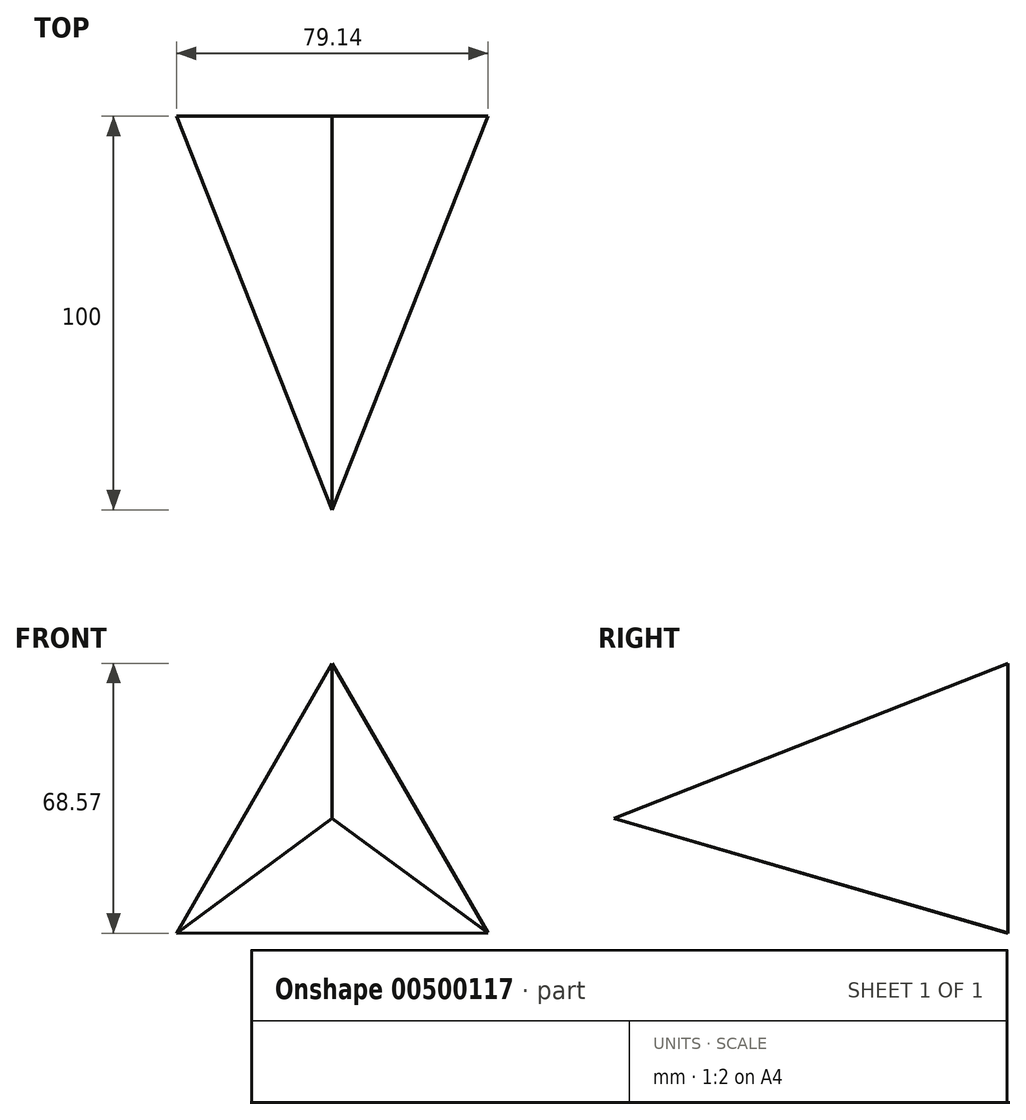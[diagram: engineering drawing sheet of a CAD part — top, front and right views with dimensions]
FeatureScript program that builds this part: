
annotation { "Feature Type Name" : "Feature", "Feature Type Description" : "" }
export const myFeature = defineFeature(function(context is Context, id is Id, definition is map)
    precondition{}
    {
        {
            var Q0;
            Q0=qCreatedBy(makeId("Front.planeOp"),FACE);
            var sketch = newSketch(context, id + "F0", { "sketchPlane" : qUnion([Q0])});
            skCircle(sketch, "E0.cCircle", {"center": v(0, 0) * mm, "radius": 45.69 * mm, "construction": true});
            skLineSegment(sketch, "E0.0", {"start": v(-0.04, 45.69) * mm, "end": v(39.6, -22.8) * mm});
            skLineSegment(sketch, "E0.1", {"start": v(39.6, -22.8) * mm, "end": v(-39.55, -22.88) * mm});
            skLineSegment(sketch, "E0.2", {"start": v(-39.55, -22.88) * mm, "end": v(-0.04, 45.69) * mm});
            skSolve(sketch);
        }
        {
            var Q0;
            Q0=qCreatedBy(makeId("Front.planeOp"),FACE);
            cPlane(context, id + "F1", {"entities" : qUnion([Q0]), "cplaneType" : CPlaneType.OFFSET, "offset" : 100 * mm, "width" : 150 * mm, "height" : 150 * mm});
        }
        {
            var Q0;
            Q0=qCreatedBy(id+"F1.planeOp",FACE);
            var sketch = newSketch(context, id + "F2", { "sketchPlane" : qUnion([Q0])});
            skPoint(sketch, "E1", {"position": v(0, 6.3) * mm});
            skSolve(sketch);
        }
        {
            var Q0;
            Q0=makeQuery(id+"F0.imprint","IMPRINT",FACE,{"disambiguationData":[TD([[makeQuery(id+"F0.imprint","IMPRINT",EDGE,{"derivedFrom":sQuery(id+"F0.wireOp",EDGE,"E0.0")}),-1.0]])]});
            var Q1;
            Q1=sQuery(id+"F2.wireOp",VERTEX,"E1");
            loft(context, id + "F3", {"sheetProfilesArray" : [{ "sheetProfileEntities" : qUnion([Q0]) }, { "sheetProfileEntities" : qUnion([Q1]) }]});
        }
    });
